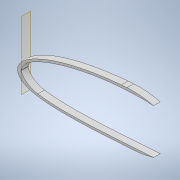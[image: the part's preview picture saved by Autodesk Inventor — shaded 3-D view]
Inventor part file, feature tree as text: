
AUTODESK INVENTOR PART (.ipt)
format: ipt  version: 2022.1 (Build 261234020, 234B)  size: 571,904 bytes
history: native  units: mm
features: sketch x7, extrude x6, thicken_offset x4, projected_geometry x3, shell x1, plane x1, other x1, fillet x1
ambient origin geometry x8: Origin, YZ Plane, XZ Plane, XY Plane, X Axis, Y Axis, Z Axis, Center Point
bodies: Solid1 (feature_tree)
feature tree (24):
  extrude  "Extrusion1"  Depth=3.0mm
  shell  "Shell1"  Thickness=1.0mm
  thicken_offset  "Thicken1"
  extrude  "Extrusion27"  TaperAngle=0.0deg  [1 undecoded]
  thicken_offset  "Thicken3"
  extrude  "Extrusion29"  Depth=20.0mm
  plane  "Work Plane5"
  other  "Bend Part2"
  thicken_offset  "Thicken5"
  extrude  "Extrusion30"  Depth=10.0mm TaperAngle=0.0deg
  extrude  "Extrusion31"  Depth=1.0mm
  thicken_offset  "Thicken6"
  extrude  "Extrusion32"  Depth=100.0mm
  fillet  "Fillet6"  Radius=5.0mm
  sketch  "Sketch3"  dims[d0=10.0mm d1=0.0mm d2=3.0mm d159=1.0mm d160=2.0mm]
  sketch  "Sketch48"  dims[d236=190.0mm d237=0.0mm d238=0.0mm]
  sketch  "Sketch55"  dims[d249=2.0mm d250=1.0mm d254=20.0mm]
  projected_geometry  "Projected Loop32"
  sketch  "Sketch57"  dims[d255=8.0mm d256=10.0mm d257=0.0mm]
  sketch  "Sketch58"  dims[d262=10.0mm d263=0.349066mm d264=1.0mm]
  projected_geometry  "Projected Loop34"
  sketch  "Sketch59"  dims[d265=1.0mm d268=100.0mm d269=5.0mm]
  sketch  "Sketch60"  dims[d270=10.0mm d271=0.0mm d272=150.0mm d273=100.0mm d274=0.0mm d275=2.5mm d276=2.0mm d277=3.0mm d278=300.0mm d279=10.0mm d280=0.0mm d281=100.0mm d282=0.0mm d283=0.0mm d284=0.0mm]
  projected_geometry  "Projected Loop35"
note: 1 required parameter value undecoded (feature->parameter linkage not recoverable at this tier; creation-order binding heuristic only, values carry confidence <= 0.55)
